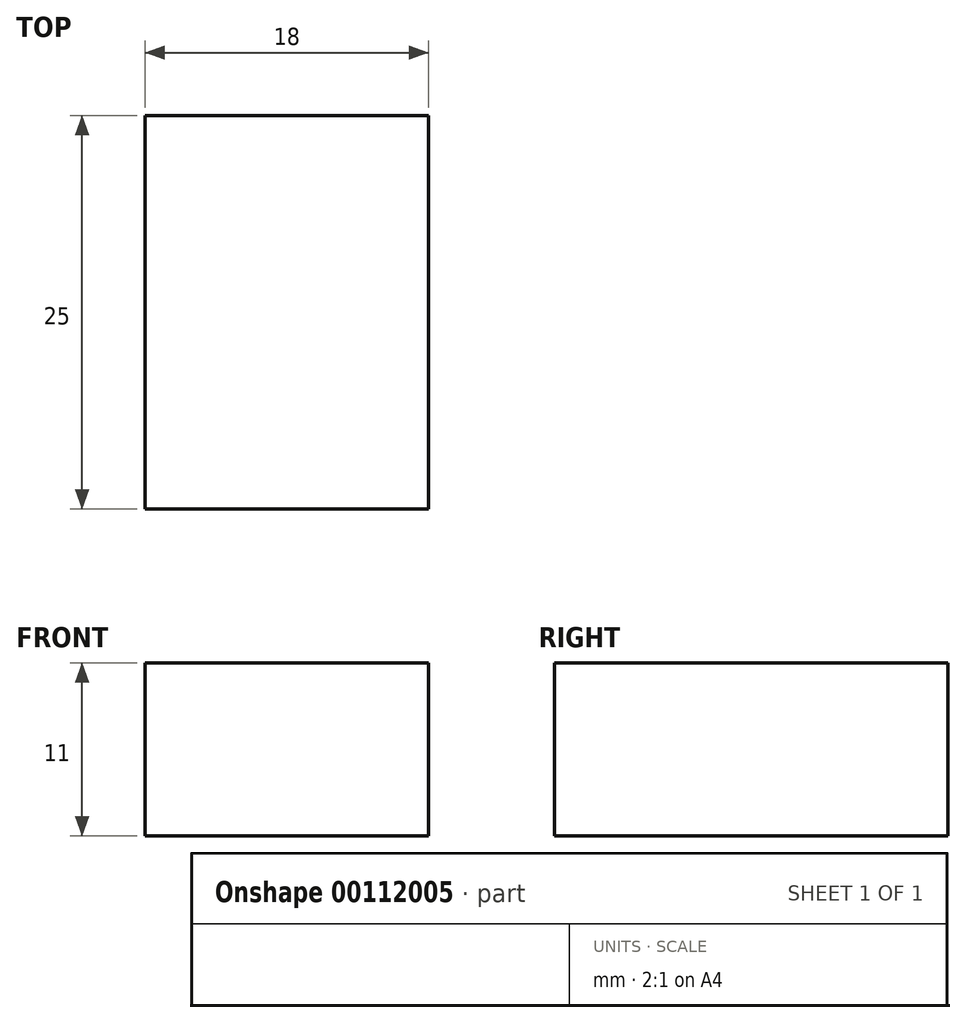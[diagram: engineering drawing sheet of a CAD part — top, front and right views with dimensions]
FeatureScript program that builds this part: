
annotation { "Feature Type Name" : "Feature", "Feature Type Description" : "" }
export const myFeature = defineFeature(function(context is Context, id is Id, definition is map)
    precondition{}
    {
        {
            var Q0;
            Q0=qCreatedBy(makeId("Top.planeOp"),FACE);
            var sketch = newSketch(context, id + "F0", { "sketchPlane" : qUnion([Q0])});
            skLineSegment(sketch, "E0.bottom", {"start": v(0, 0) * mm, "end": v(18, 0) * mm});
            skLineSegment(sketch, "E0.top", {"start": v(0, -25) * mm, "end": v(18, -25) * mm});
            skLineSegment(sketch, "E0.left", {"start": v(0, 0) * mm, "end": v(0, -25) * mm});
            skLineSegment(sketch, "E0.right", {"start": v(18, 0) * mm, "end": v(18, -25) * mm});
            skSolve(sketch);
        }
        {
            var Q0;
            Q0 = qSketchRegion(id + "F0", true);
            extrude(context, id + "F1", {"entities" : qUnion([Q0]), "depth" : 11 * mm});
        }
    });
